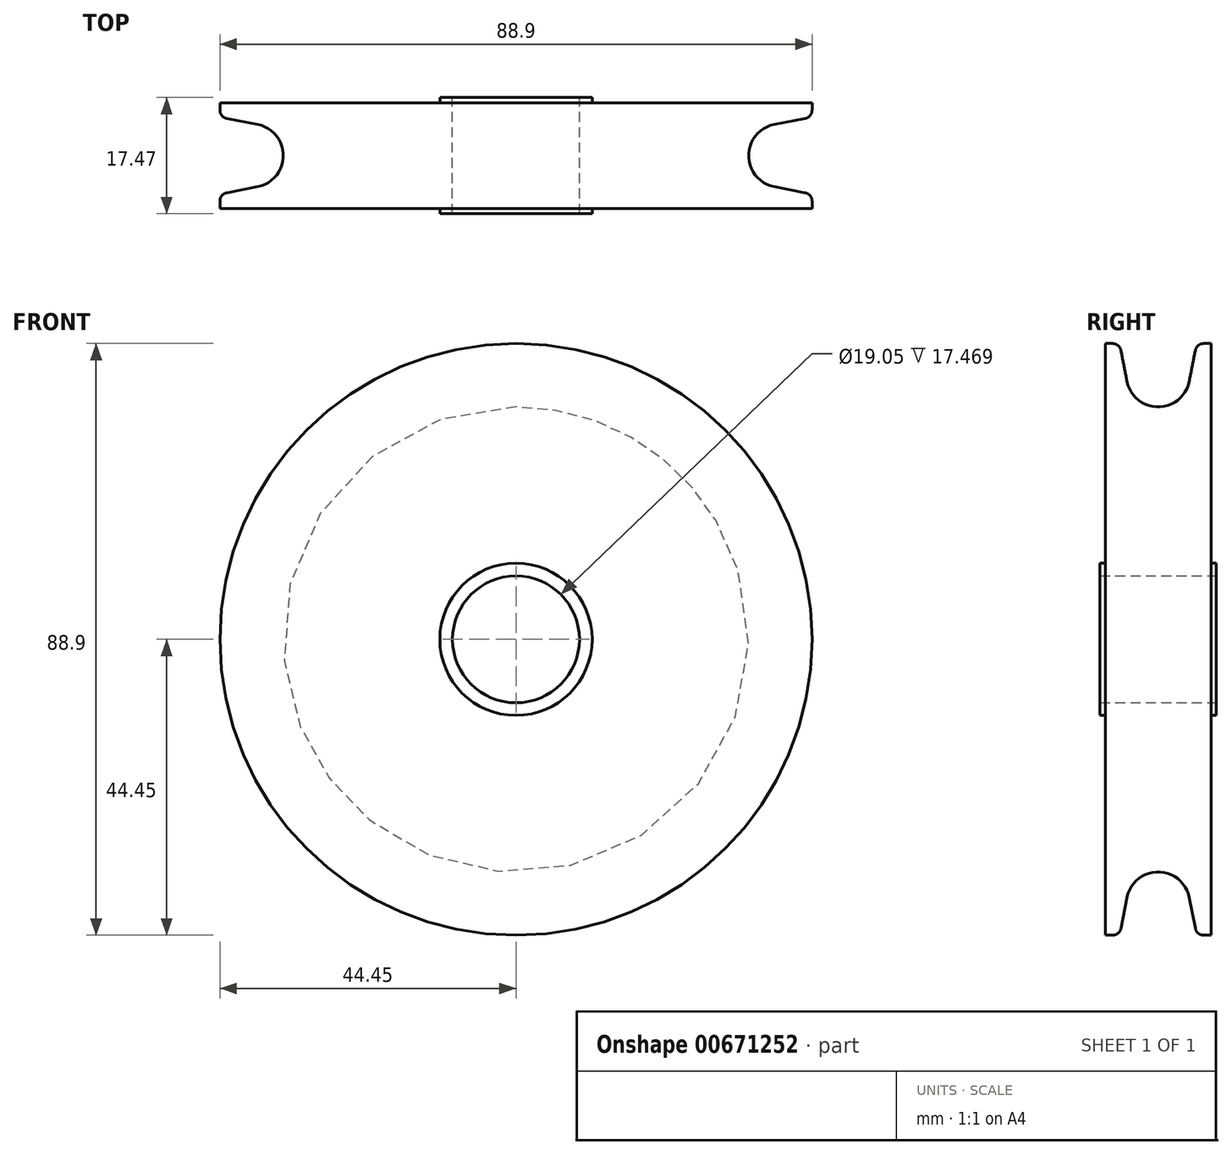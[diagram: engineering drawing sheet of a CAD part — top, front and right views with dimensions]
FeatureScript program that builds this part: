
annotation { "Feature Type Name" : "Feature", "Feature Type Description" : "" }
export const myFeature = defineFeature(function(context is Context, id is Id, definition is map)
    precondition{}
    {
        {
            var Q0;
            Q0=qCreatedBy(makeId("Front.planeOp"),FACE);
            var sketch = newSketch(context, id + "F0", { "sketchPlane" : qUnion([Q0])});
            skCircle(sketch, "E0", {"center": v(0, 0) * mm, "radius": 9.53 * mm});
            skCircle(sketch, "E1", {"center": v(0, 0) * mm, "radius": 44.45 * mm});
            skCircle(sketch, "E2", {"center": v(0, 0) * mm, "radius": 11.43 * mm});
            skSolve(sketch);
        }
        {
            var Q0;
            Q0=makeQuery(id+"F0.imprint","IMPRINT",FACE,{"disambiguationData":[TD([[makeQuery(id+"F0.imprint","IMPRINT",EDGE,{"derivedFrom":sQuery(id+"F0.wireOp",EDGE,"E0")}),-1.0]])]});
            extrude(context, id + "F1", {"entities" : qUnion([Q0]), "depth" : 8.73 * mm, "offsetDistance" : 25.4 * mm, "hasSecondDirection" : true, "secondDirectionOppositeDirection" : true, "secondDirectionDepth" : 8.74 * mm});
        }
        {
            var Q0;
            Q0=qSketchRegion(id+"F0",true);
            extrude(context, id + "F2", {"entities" : qUnion([Q0]), "operationType" : NewBodyOperationType.ADD, "depth" : 7.94 * mm, "offsetDistance" : 25.4 * mm, "hasSecondDirection" : true, "secondDirectionOppositeDirection" : true, "secondDirectionDepth" : 7.95 * mm});
        }
        {
            var Q0;
            Q0=qCreatedBy(makeId("Right.planeOp"),FACE);
            var sketch = newSketch(context, id + "F3", { "sketchPlane" : qUnion([Q0])});
            skArc(sketch, "E3", {"start": v(-4.67, 38.77) * mm, "mid": v(0, 34.92) * mm, "end": v(4.67, 38.77) * mm});
            skLineSegment(sketch, "E4", {"start": v(-6.35, 47.3) * mm, "end": v(6.35, 47.3) * mm});
            skLineSegment(sketch, "E5", {"start": v(0, 39.69) * mm, "end": v(0, 47.3) * mm});
            skLineSegment(sketch, "E6", {"start": v(6.35, 47.3) * mm, "end": v(4.67, 38.77) * mm});
            skLineSegment(sketch, "E7", {"start": v(-6.35, 47.3) * mm, "end": v(-4.67, 38.77) * mm});
            skLineSegment(sketch, "E8", {"start": v(0, 0) * mm, "end": v(67.78, 0) * mm});
            skSolve(sketch);
        }
        {
            var Q0;
            Q0=makeQuery(id+"F3.imprint","IMPRINT",FACE,{"disambiguationData":[TD([[makeQuery(id+"F3.imprint","IMPRINT",EDGE,{"derivedFrom":sQuery(id+"F3.wireOp",EDGE,"E3")}),1.0]])]});
            var Q1;
            Q1=sQuery(id+"F3.wireOp",EDGE,"E8");
            revolve(context, id + "F4", {"operationType" : NewBodyOperationType.REMOVE, "surfaceOperationType" : NewSurfaceOperationType.NEW, "entities" : qUnion([Q0]), "axis" : qUnion([Q1]), "revolveType" : RevolveType.FULL, "oppositeDirection" : true});
        }
        {
            var Q0;
            Q0=makeQuery(id+"F4.boolean.opBoolean","INTERSECT",EDGE,{"derivedFrom":[makeQuery(id+"F2.opExtrude","SWEPT_FACE",FACE,{"disambiguationData":[OSD([sQuery(id+"F0.wireOp",EDGE,"E1")])]}),makeQuery(id+"F4.opRevolve","SWEPT_FACE",FACE,{"disambiguationData":[OSD([sQuery(id+"F3.wireOp",EDGE,"E7")])]})]});
            var Q1;
            Q1=makeQuery(id+"F4.boolean.opBoolean","INTERSECT",EDGE,{"derivedFrom":[makeQuery(id+"F2.opExtrude","SWEPT_FACE",FACE,{"disambiguationData":[OSD([sQuery(id+"F0.wireOp",EDGE,"E1")])]}),makeQuery(id+"F4.opRevolve","SWEPT_FACE",FACE,{"disambiguationData":[OSD([sQuery(id+"F3.wireOp",EDGE,"E6")])]})]});
            fillet(context, id + "F5", {"entities" : qUnion([Q0, Q1]), "radius" : 1.27 * mm, "tangentPropagation" : true, "allowEdgeOverflow" : false});
        }
    });
